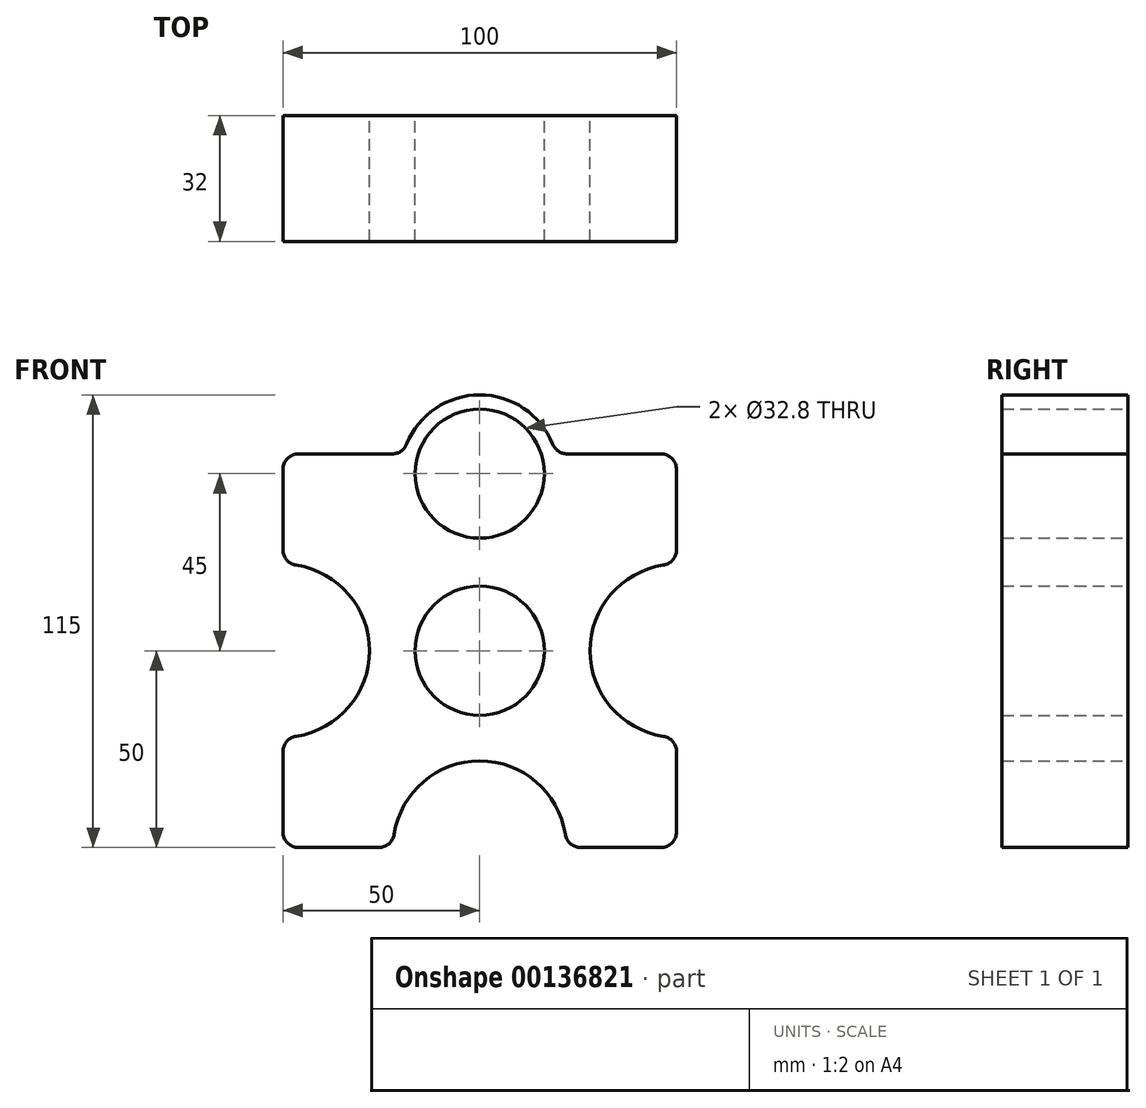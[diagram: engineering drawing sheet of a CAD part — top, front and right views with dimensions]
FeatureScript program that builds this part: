
annotation { "Feature Type Name" : "Feature", "Feature Type Description" : "" }
export const myFeature = defineFeature(function(context is Context, id is Id, definition is map)
    precondition{}
    {
        {
            var Q0;
            Q0=qCreatedBy(makeId("Front.planeOp"),FACE);
            var sketch = newSketch(context, id + "F0", { "sketchPlane" : qUnion([Q0])});
            skLineSegment(sketch, "E0.bottom", {"start": v(50, -50) * mm, "end": v(22, -50) * mm});
            skLineSegment(sketch, "E0.top", {"start": v(50, 50) * mm, "end": v(19.36, 50) * mm});
            skLineSegment(sketch, "E0.left", {"start": v(50, -50) * mm, "end": v(50, -22) * mm});
            skLineSegment(sketch, "E0.right", {"start": v(-50, -50) * mm, "end": v(-50, -22) * mm});
            skPoint(sketch, "E0.middle", {"position": v(0, 0) * mm});
            skCircle(sketch, "E1", {"center": v(0, 0) * mm, "radius": 16.4 * mm});
            skArc(sketch, "E2", {"start": v(22, -50) * mm, "mid": v(0, -28) * mm, "end": v(-22, -50) * mm});
            skArc(sketch, "E3", {"start": v(-50, -22) * mm, "mid": v(-28, 0) * mm, "end": v(-50, 22) * mm});
            skArc(sketch, "E4", {"start": v(50, 22) * mm, "mid": v(28, 0) * mm, "end": v(50, -22) * mm});
            skArc(sketch, "E5", {"start": v(19.36, 50) * mm, "mid": v(0, 65) * mm, "end": v(-19.36, 50) * mm});
            skCircle(sketch, "E6", {"center": v(0, 45) * mm, "radius": 16.4 * mm});
            skLineSegment(sketch, "E7.trimOffspring", {"start": v(-50, 22) * mm, "end": v(-50, 50) * mm});
            skLineSegment(sketch, "E8.trimOffspring", {"start": v(-22, -50) * mm, "end": v(-50, -50) * mm});
            skLineSegment(sketch, "E9.trimOffspring", {"start": v(50, 22) * mm, "end": v(50, 50) * mm});
            skLineSegment(sketch, "E10.trimOffspring", {"start": v(-19.36, 50) * mm, "end": v(-50, 50) * mm});
            skSolve(sketch);
        }
        {
            var Q0;
            Q0 = qSketchRegion(id + "F0", true);
            var Q1;
            Q1=makeQuery(id+"F0.imprint","IMPRINT",FACE,{"disambiguationData":[TD([[makeQuery(id+"F0.imprint","IMPRINT",EDGE,{"derivedFrom":sQuery(id+"F0.wireOp",EDGE,"E0.bottom")}),-1.0]])]});
            extrude(context, id + "F1", {"entities" : qUnion([Q0, Q1]), "endBound" : BoundingType.SYMMETRIC, "depth" : 32 * mm});
        }
        {
            var Q0;
            Q0=makeQuery(id+"F1.opExtrude","SWEPT_EDGE",EDGE,{"disambiguationData":[OSD([sQuery(id+"F0.wireOp",EDGE,"E0.top"),sQuery(id+"F0.wireOp",EDGE,"E5")])]});
            var Q1;
            Q1=makeQuery(id+"F1.opExtrude","SWEPT_EDGE",EDGE,{"disambiguationData":[OSD([sQuery(id+"F0.wireOp",EDGE,"E0.top"),sQuery(id+"F0.wireOp",EDGE,"E9.trimOffspring")])]});
            var Q2;
            Q2=makeQuery(id+"F1.opExtrude","SWEPT_EDGE",EDGE,{"disambiguationData":[OSD([sQuery(id+"F0.wireOp",EDGE,"E4"),sQuery(id+"F0.wireOp",EDGE,"E9.trimOffspring")])]});
            var Q3;
            Q3=makeQuery(id+"F1.opExtrude","SWEPT_EDGE",EDGE,{"disambiguationData":[OSD([sQuery(id+"F0.wireOp",EDGE,"E0.left"),sQuery(id+"F0.wireOp",EDGE,"E4")])]});
            var Q4;
            Q4=makeQuery(id+"F1.opExtrude","SWEPT_EDGE",EDGE,{"disambiguationData":[OSD([sQuery(id+"F0.wireOp",EDGE,"E0.bottom"),sQuery(id+"F0.wireOp",EDGE,"E0.left")])]});
            var Q5;
            Q5=makeQuery(id+"F1.opExtrude","SWEPT_EDGE",EDGE,{"disambiguationData":[OSD([sQuery(id+"F0.wireOp",EDGE,"E0.right"),sQuery(id+"F0.wireOp",EDGE,"E3")])]});
            var Q6;
            Q6=makeQuery(id+"F1.opExtrude","SWEPT_EDGE",EDGE,{"disambiguationData":[OSD([sQuery(id+"F0.wireOp",EDGE,"E7.trimOffspring"),sQuery(id+"F0.wireOp",EDGE,"E10.trimOffspring")])]});
            var Q7;
            Q7=makeQuery(id+"F1.opExtrude","SWEPT_EDGE",EDGE,{"disambiguationData":[OSD([sQuery(id+"F0.wireOp",EDGE,"E5"),sQuery(id+"F0.wireOp",EDGE,"E10.trimOffspring")])]});
            var Q8;
            Q8=makeQuery(id+"F1.opExtrude","SWEPT_EDGE",EDGE,{"disambiguationData":[OSD([sQuery(id+"F0.wireOp",EDGE,"E3"),sQuery(id+"F0.wireOp",EDGE,"E7.trimOffspring")])]});
            var Q9;
            Q9=makeQuery(id+"F1.opExtrude","SWEPT_EDGE",EDGE,{"disambiguationData":[OSD([sQuery(id+"F0.wireOp",EDGE,"E0.right"),sQuery(id+"F0.wireOp",EDGE,"E8.trimOffspring")])]});
            var Q10;
            Q10=makeQuery(id+"F1.opExtrude","SWEPT_EDGE",EDGE,{"disambiguationData":[OSD([sQuery(id+"F0.wireOp",EDGE,"E0.bottom"),sQuery(id+"F0.wireOp",EDGE,"E2")])]});
            var Q11;
            Q11=makeQuery(id+"F1.opExtrude","SWEPT_EDGE",EDGE,{"disambiguationData":[OSD([sQuery(id+"F0.wireOp",EDGE,"E2"),sQuery(id+"F0.wireOp",EDGE,"E8.trimOffspring")])]});
            fillet(context, id + "F2", {"entities" : qUnion([Q0, Q1, Q2, Q3, Q4, Q5, Q6, Q7, Q8, Q9, Q10, Q11]), "radius" : 4 * mm, "tangentPropagation" : true, "allowEdgeOverflow" : false});
        }
    });
